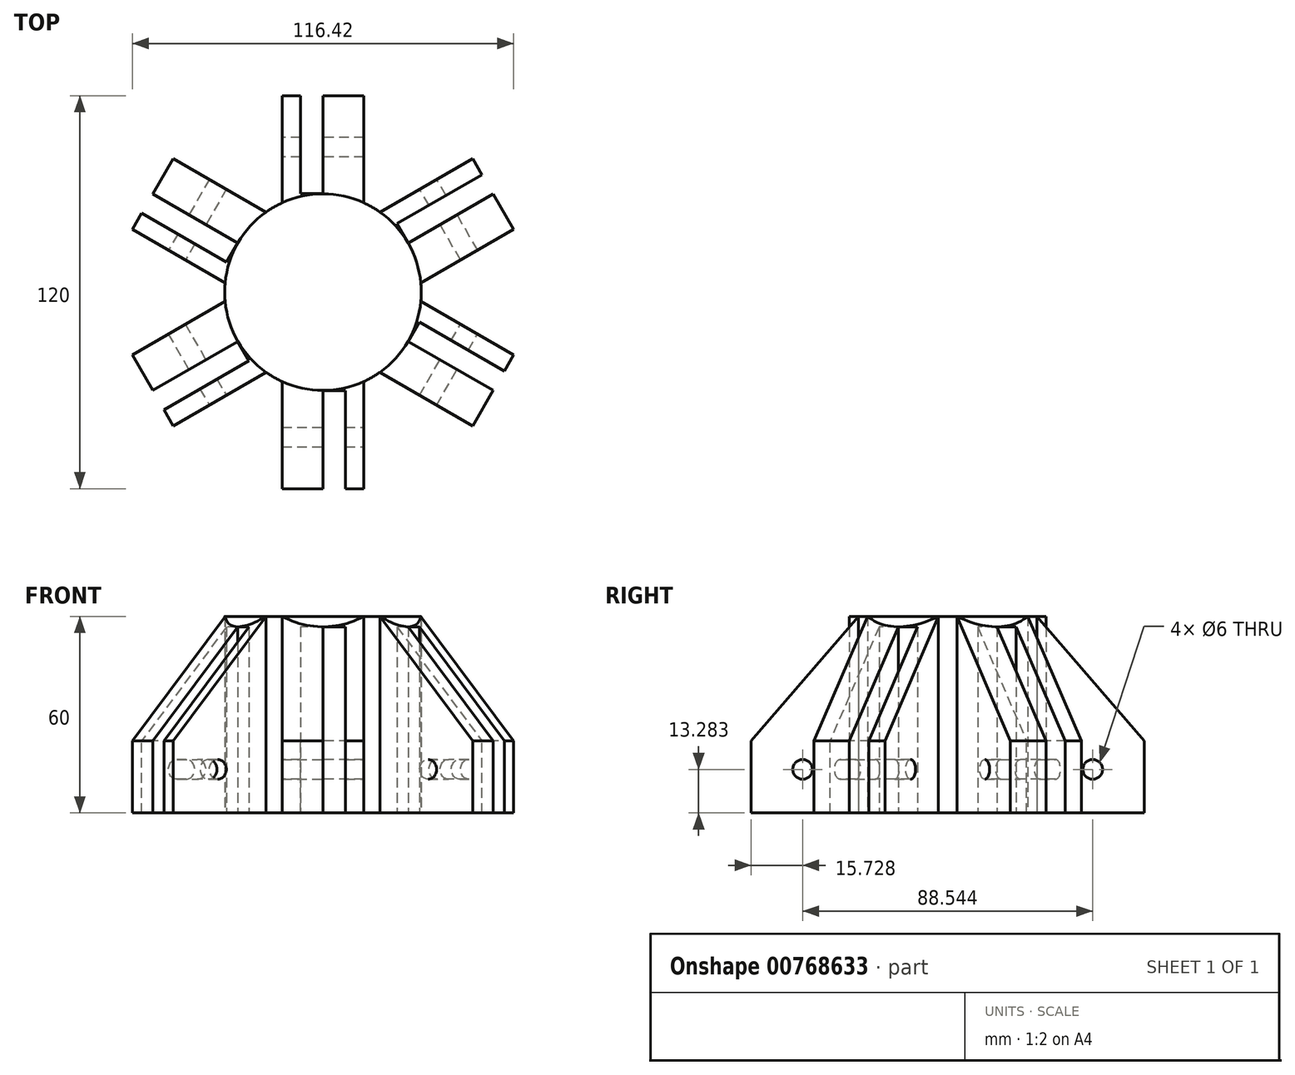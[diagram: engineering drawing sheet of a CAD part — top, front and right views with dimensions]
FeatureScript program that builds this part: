
annotation { "Feature Type Name" : "Feature", "Feature Type Description" : "" }
export const myFeature = defineFeature(function(context is Context, id is Id, definition is map)
    precondition{}
    {
        {
            var Q0;
            Q0=qCreatedBy(makeId("Top.planeOp"),FACE);
            var sketch = newSketch(context, id + "F0", { "sketchPlane" : qUnion([Q0])});
            skCircle(sketch, "E0", {"center": v(0, 0) * mm, "radius": 30 * mm});
            skSolve(sketch);
        }
        {
            var Q0;
            Q0 = qSketchRegion(id + "F0", true);
            var Q1;
            Q1 = qSketchRegion(id + "F2", true);
            extrude(context, id + "F1", {"entities" : qUnion([Q0, Q1]), "depth" : 60 * mm, "offsetDistance" : 25 * mm});
        }
        {
            var Q0;
            Q0=qCreatedBy(makeId("Front.planeOp"),FACE);
            var sketch = newSketch(context, id + "F2", { "sketchPlane" : qUnion([Q0])});
            skLineSegment(sketch, "E1.bottom", {"start": v(-12.5, 0) * mm, "end": v(12.5, 0) * mm});
            skLineSegment(sketch, "E1.top", {"start": v(-12.5, 60) * mm, "end": v(12.5, 60) * mm});
            skLineSegment(sketch, "E1.left", {"start": v(-12.5, 0) * mm, "end": v(-12.5, 60) * mm});
            skLineSegment(sketch, "E1.right", {"start": v(12.5, 0) * mm, "end": v(12.5, 60) * mm});
            skSolve(sketch);
        }
        {
            var Q0;
            Q0 = qSketchRegion(id + "F2", true);
            var Q1;
            Q1 = qSketchRegion(id + "F4", true);
            extrude(context, id + "F3", {"entities" : qUnion([Q0, Q1]), "operationType" : NewBodyOperationType.ADD, "depth" : 60 * mm, "offsetDistance" : 25 * mm});
        }
        {
            var Q0;
            Q0=makeQuery(id+"F3.opExtrude","SWEPT_FACE",FACE,{"disambiguationData":[OSD([sQuery(id+"F2.wireOp",EDGE,"E1.right")])]});
            var sketch = newSketch(context, id + "F4", { "sketchPlane" : qUnion([Q0])});
            skLineSegment(sketch, "E2", {"start": v(-27.27, 60) * mm, "end": v(-60, 21.96) * mm});
            skLineSegment(sketch, "E3", {"start": v(-60, 21.96) * mm, "end": v(-60, 60) * mm});
            skLineSegment(sketch, "E4", {"start": v(-60, 60) * mm, "end": v(-27.27, 60) * mm});
            skSolve(sketch);
        }
        {
            var Q0;
            Q0 = qSketchRegion(id + "F4", true);
            var Q1;
            Q1 = qSketchRegion(id + "FgFtPWKNHrMfXQx_1", true);
            extrude(context, id + "F5", {"entities" : qUnion([Q0, Q1]), "operationType" : NewBodyOperationType.REMOVE, "oppositeDirection" : true, "depth" : 25 * mm, "offsetDistance" : 25 * mm});
        }
        {
            var Q0;
            Q0=qCreatedBy(makeId("Top.planeOp"),FACE);
            var sketch = newSketch(context, id + "F6", { "sketchPlane" : qUnion([Q0])});
            skLineSegment(sketch, "E5.bottom", {"start": v(0, -30.09) * mm, "end": v(6.81, -30.09) * mm});
            skLineSegment(sketch, "E5.top", {"start": v(0, -66.74) * mm, "end": v(6.81, -66.74) * mm});
            skLineSegment(sketch, "E5.left", {"start": v(0, -30.09) * mm, "end": v(0, -66.74) * mm});
            skLineSegment(sketch, "E5.right", {"start": v(6.81, -30.09) * mm, "end": v(6.81, -66.74) * mm});
            skSolve(sketch);
        }
        {
            var Q0;
            Q0 = qSketchRegion(id + "F6", true);
            var Q1;
            Q1=makeQuery(id+"F5.boolean.opBoolean","COPY",FACE,{"derivedFrom":makeQuery(id+"F5.opExtrude","SWEPT_FACE",FACE,{"disambiguationData":[OSD([sQuery(id+"F4.wireOp",EDGE,"E2")])]})});
            extrude(context, id + "F7", {"entities" : qUnion([Q0, Q1]), "operationType" : NewBodyOperationType.REMOVE, "depth" : 114.6 * mm, "offsetDistance" : 25 * mm});
        }
        {
            var Q0;
            Q0=makeQuery(id+"F3.opExtrude","SWEPT_FACE",FACE,{"disambiguationData":[OSD([sQuery(id+"F2.wireOp",EDGE,"E1.right")])]});
            var sketch = newSketch(context, id + "F8", { "sketchPlane" : qUnion([Q0])});
            skCircle(sketch, "E6", {"center": v(-44.27, 13.28) * mm, "radius": 3 * mm});
            skSolve(sketch);
        }
        {
            var Q0;
            Q0=sQuery(id+"F8.wireOp",VERTEX,"E6.center");
            var Q1;
            Q1=makeQuery(id+"F1.opExtrude","SWEPT_BODY",BODY,{"disambiguationData":[OSD([sQuery(id+"F0.wireOp",EDGE,"E0")])]});
            hole(context, id + "F9", {"style" : HoleStyle.SIMPLE, "endStyle" : HoleEndStyle.THROUGH, "holeDiameter" : 6 * mm, "majorDiameter" : 5 * mm, "isTappedThrough" : true, "tappedDepth" : 12 * mm, "tapClearance" : 3, "locations" : qUnion([Q0]), "scope" : qUnion([Q1])});
        }
        {
            var Q0;
            Q0=makeQuery(id+"F1.opExtrude","SWEPT_BODY",BODY,{"disambiguationData":[OSD([sQuery(id+"F0.wireOp",EDGE,"E0")])]});
            var Q1;
            Q1=makeQuery(id+"F1.opExtrude","SWEPT_FACE",FACE,{"disambiguationData":[OSD([sQuery(id+"F0.wireOp",EDGE,"E0")])]});
            circularPattern(context, id + "F10", {"operationType" : NewBodyOperationType.ADD, "entities" : qUnion([Q0]), "axis" : qUnion([Q1]), "angle" : 360 * degree, "instanceCount" : 6, "equalSpace" : true});
        }
    });
